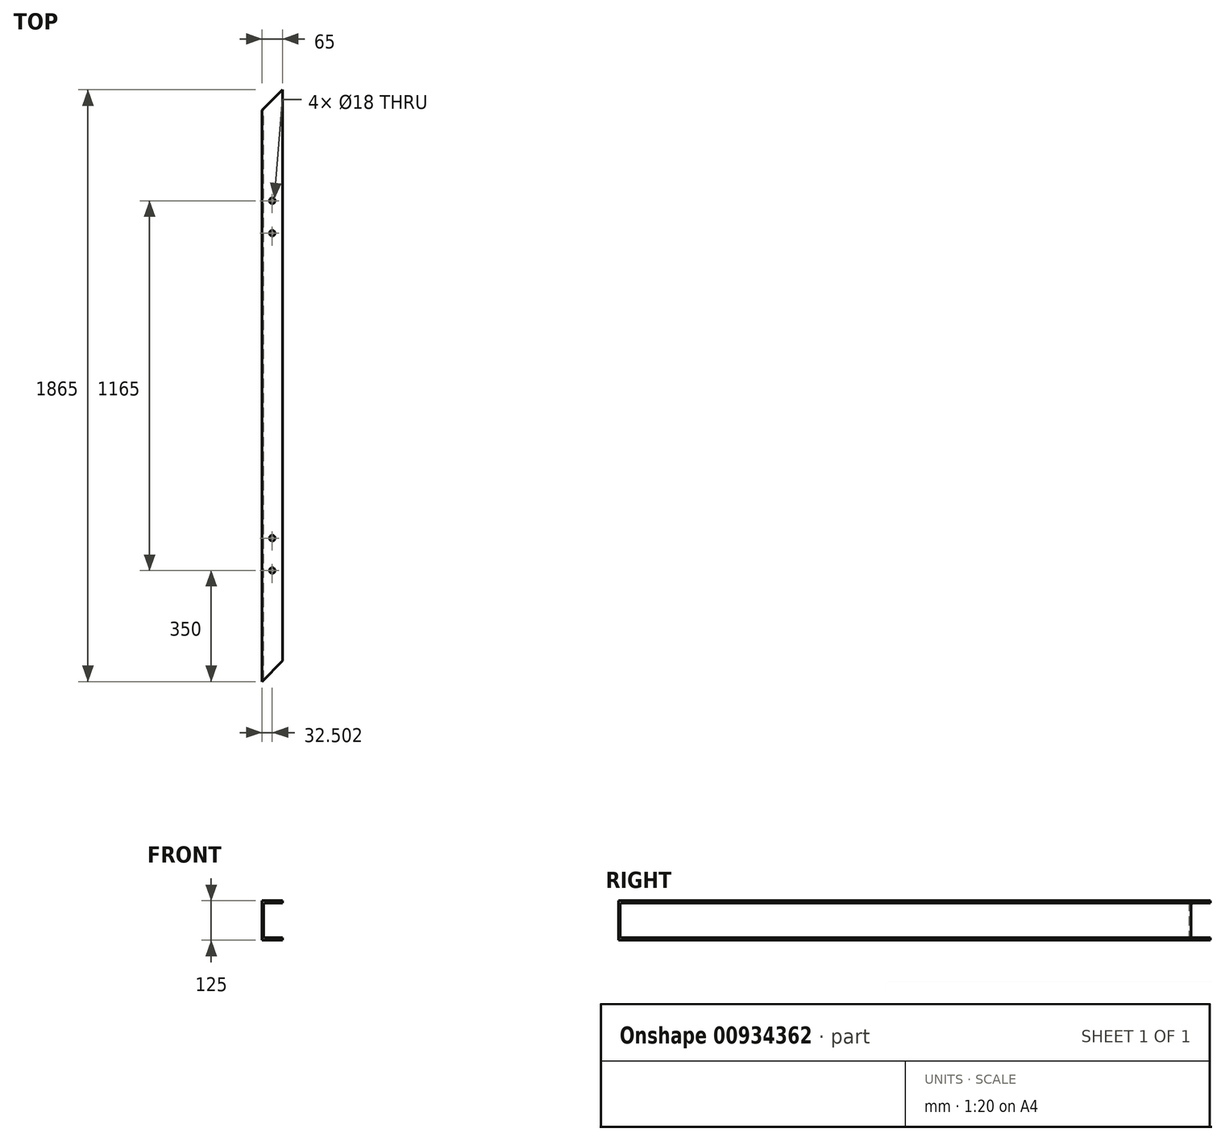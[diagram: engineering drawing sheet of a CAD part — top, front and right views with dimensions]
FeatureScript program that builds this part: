
annotation { "Feature Type Name" : "Feature", "Feature Type Description" : "" }
export const myFeature = defineFeature(function(context is Context, id is Id, definition is map)
    precondition{}
    {
        {
            var Q0;
            Q0=qCreatedBy(makeId("Front.planeOp"),FACE);
            var sketch = newSketch(context, id + "F0", { "sketchPlane" : qUnion([Q0])});
            skLineSegment(sketch, "E0", {"start": v(-25.17, -62.5) * mm, "end": v(-25.17, 62.5) * mm});
            skLineSegment(sketch, "E1", {"start": v(-25.17, 62.5) * mm, "end": v(39.83, 62.5) * mm});
            skLineSegment(sketch, "E2", {"start": v(39.83, 62.5) * mm, "end": v(39.83, 55) * mm});
            skLineSegment(sketch, "E3", {"start": v(39.83, 55) * mm, "end": v(-12.47, 55) * mm});
            skLineSegment(sketch, "E4", {"start": v(-25.17, -62.5) * mm, "end": v(39.83, -62.5) * mm});
            skLineSegment(sketch, "E5", {"start": v(39.83, -62.5) * mm, "end": v(39.83, -55) * mm});
            skLineSegment(sketch, "E6", {"start": v(39.83, -55) * mm, "end": v(-12.47, -55) * mm});
            skLineSegment(sketch, "E7", {"start": v(-20.47, -47) * mm, "end": v(-20.47, 47) * mm});
            skPoint(sketch, "E8.visualSharp", {"position": v(-20.47, 55) * mm});
            skArc(sketch, "E8.filletArc", {"start": v(-12.47, 55) * mm, "mid": v(-18.12, 52.66) * mm, "end": v(-20.47, 47) * mm});
            skPoint(sketch, "E9.visualSharp", {"position": v(-20.47, -55) * mm});
            skArc(sketch, "E9.filletArc", {"start": v(-20.47, -47) * mm, "mid": v(-18.12, -52.66) * mm, "end": v(-12.47, -55) * mm});
            skSolve(sketch);
        }
        {
            var Q0;
            Q0=makeQuery(id+"F0.imprint","IMPRINT",FACE,{"disambiguationData":[TD([[makeQuery(id+"F0.imprint","IMPRINT",EDGE,{"derivedFrom":sQuery(id+"F0.wireOp",EDGE,"E0")}),-1.0]])]});
            extrude(context, id + "F1", {"entities" : qUnion([Q0]), "depth" : 1865 * mm, "offsetDistance" : 25 * mm});
        }
        {
            var Q0;
            Q0=makeQuery(id+"F1.opExtrude","SWEPT_FACE",FACE,{"disambiguationData":[OSD([sQuery(id+"F0.wireOp",EDGE,"E1")])]});
            var sketch = newSketch(context, id + "F2", { "sketchPlane" : qUnion([Q0])});
            skLineSegment(sketch, "E10", {"start": v(-25.17, 0) * mm, "end": v(-25.17, -65) * mm});
            skLineSegment(sketch, "E11", {"start": v(-25.17, -65) * mm, "end": v(39.83, 0) * mm});
            skLineSegment(sketch, "E12", {"start": v(39.83, -1865) * mm, "end": v(39.83, -1800) * mm});
            skLineSegment(sketch, "E13", {"start": v(39.83, -1800) * mm, "end": v(-25.17, -1865) * mm});
            skSolve(sketch);
        }
        {
            var Q0;
            Q0=makeQuery(id+"F2.imprint","IMPRINT",FACE,{"disambiguationData":[TD([[makeQuery(id+"F2.imprint","IMPRINT",EDGE,{"derivedFrom":sQuery(id+"F2.wireOp",EDGE,"E12")}),1.0]])]});
            var Q1;
            Q1=makeQuery(id+"F2.imprint","IMPRINT",FACE,{"disambiguationData":[TD([[makeQuery(id+"F2.imprint","IMPRINT",EDGE,{"derivedFrom":sQuery(id+"F2.wireOp",EDGE,"E10")}),-1.0]])]});
            extrude(context, id + "F3", {"entities" : qUnion([Q0, Q1]), "operationType" : NewBodyOperationType.REMOVE, "endBound" : BoundingType.THROUGH_ALL, "oppositeDirection" : true, "depth" : 25 * mm, "offsetDistance" : 25 * mm});
        }
        {
            var Q0;
            Q0=makeQuery(id+"F1.opExtrude","SWEPT_FACE",FACE,{"disambiguationData":[OSD([sQuery(id+"F0.wireOp",EDGE,"E1")])]});
            var sketch = newSketch(context, id + "F4", { "sketchPlane" : qUnion([Q0])});
            skCircle(sketch, "E14", {"center": v(7.33, -350) * mm, "radius": 9 * mm});
            skCircle(sketch, "E15", {"center": v(7.33, -452) * mm, "radius": 9 * mm});
            skCircle(sketch, "E16", {"center": v(7.33, -1515) * mm, "radius": 9 * mm});
            skCircle(sketch, "E17", {"center": v(7.33, -1413) * mm, "radius": 9 * mm});
            skSolve(sketch);
        }
        {
            var Q0;
            Q0 = qSketchRegion(id + "F4", true);
            extrude(context, id + "F5", {"entities" : qUnion([Q0]), "operationType" : NewBodyOperationType.REMOVE, "endBound" : BoundingType.UP_TO_NEXT, "oppositeDirection" : true, "depth" : 25 * mm, "offsetDistance" : 25 * mm});
        }
    });
